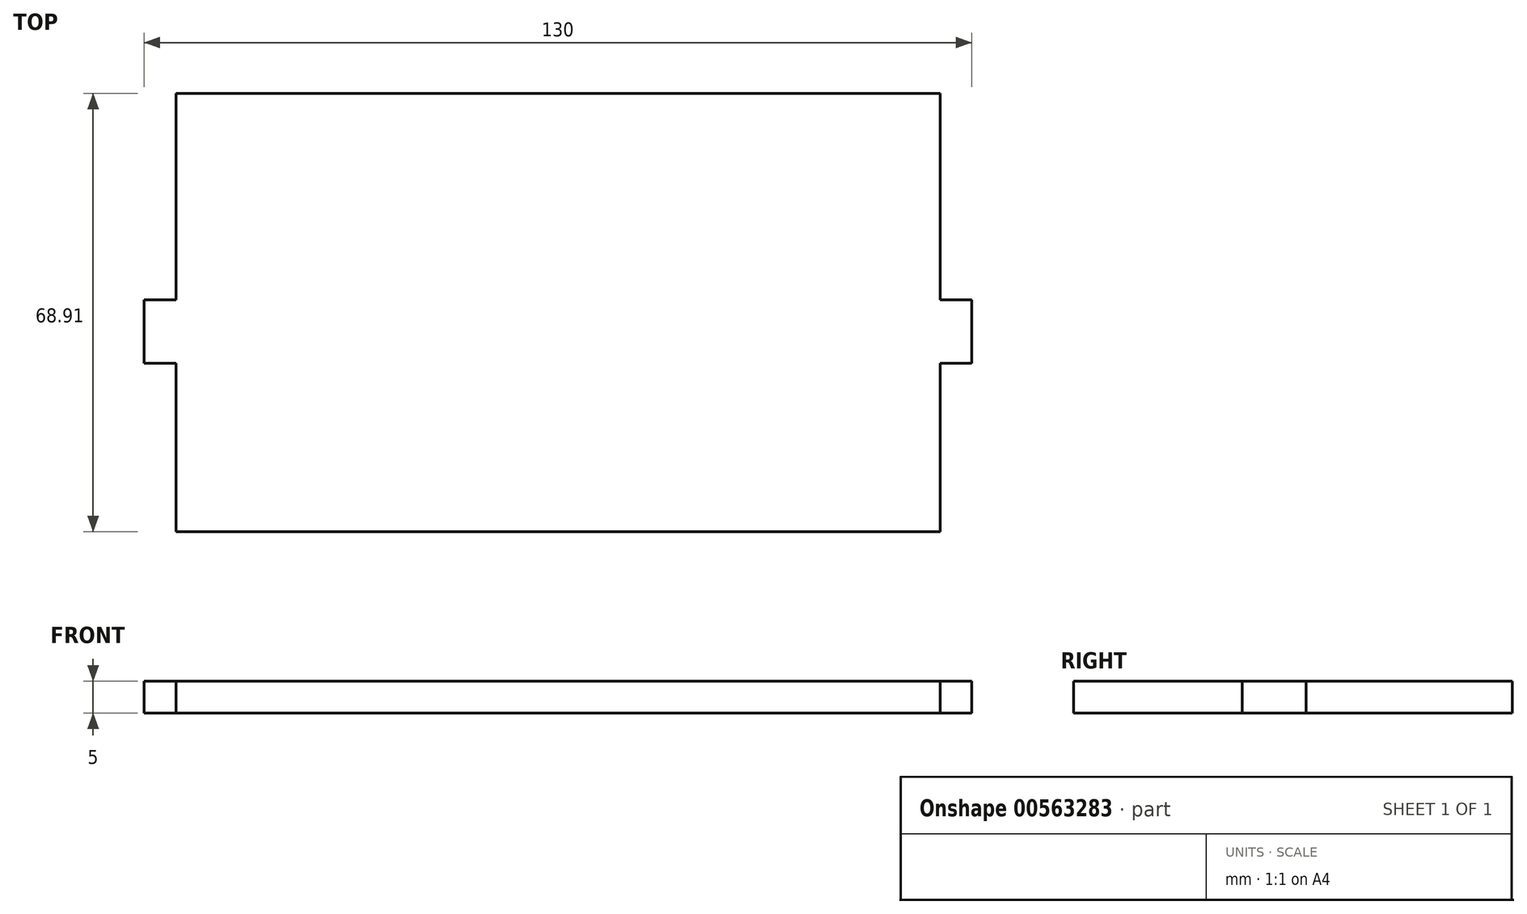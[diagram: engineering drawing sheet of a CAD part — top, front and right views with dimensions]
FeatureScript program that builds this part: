
annotation { "Feature Type Name" : "Feature", "Feature Type Description" : "" }
export const myFeature = defineFeature(function(context is Context, id is Id, definition is map)
    precondition{}
    {
        {
            var Q0;
            Q0=qCreatedBy(makeId("Top.planeOp"),FACE);
            var sketch = newSketch(context, id + "F0", { "sketchPlane" : qUnion([Q0])});
            skLineSegment(sketch, "E0.top", {"start": v(0, 74.94) * mm, "end": v(120, 74.94) * mm});
            skLineSegment(sketch, "E0.left", {"start": v(0, 6.03) * mm, "end": v(0, 32.5) * mm});
            skLineSegment(sketch, "E0.right", {"start": v(120, 6.03) * mm, "end": v(120, 32.5) * mm});
            skLineSegment(sketch, "E1.bottom", {"start": v(120, 32.5) * mm, "end": v(125, 32.5) * mm});
            skLineSegment(sketch, "E1.top", {"start": v(120, 42.5) * mm, "end": v(125, 42.5) * mm});
            skLineSegment(sketch, "E1.right", {"start": v(125, 32.5) * mm, "end": v(125, 42.5) * mm});
            skLineSegment(sketch, "E2.bottom", {"start": v(0, 32.5) * mm, "end": v(-5, 32.5) * mm});
            skLineSegment(sketch, "E2.top", {"start": v(0, 42.5) * mm, "end": v(-5, 42.5) * mm});
            skLineSegment(sketch, "E2.right", {"start": v(-5, 32.5) * mm, "end": v(-5, 42.5) * mm});
            skLineSegment(sketch, "E3.trimOffspring", {"start": v(0, 42.5) * mm, "end": v(0, 74.94) * mm});
            skLineSegment(sketch, "E4.top", {"start": v(0, 6.03) * mm, "end": v(120, 6.03) * mm});
            skLineSegment(sketch, "E5.trimOffspring", {"start": v(120, 42.5) * mm, "end": v(120, 74.94) * mm});
            skSolve(sketch);
        }
        {
            var Q0;
            Q0=makeQuery(id+"F0.imprint","IMPRINT",FACE,{"disambiguationData":[TD([[makeQuery(id+"F0.imprint","IMPRINT",EDGE,{"derivedFrom":sQuery(id+"F0.wireOp",EDGE,"E0.top")}),-1.0]])]});
            extrude(context, id + "F1", {"entities" : qUnion([Q0]), "depth" : 5 * mm, "offsetDistance" : 25 * mm});
        }
    });
